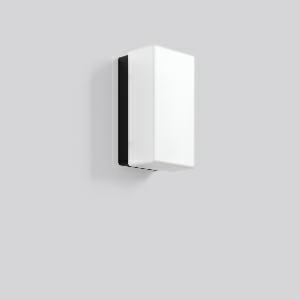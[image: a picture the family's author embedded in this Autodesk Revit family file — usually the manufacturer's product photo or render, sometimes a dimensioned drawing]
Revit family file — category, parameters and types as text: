
# Revit family: rechteck_21146_003_5e70
name_source: partatom
category: Lighting Fixtures
units: mm (PartAtom-declared; Revit-internal decimal feet)

## family parameters
Cut with Voids When Loaded = No
Host = Face
Light Source = No
Part Type = Normal
Room Calculation Point = No
Round Connector Dimension = Use Diameter
Shared = No

## types (1)
- RECHTECK (1 x QA60/clear E27, 700 lm, 46 W, 3000)
    Apparent Load = 46 VA
    CIE Flux Codes = 35 64 86 74 50
    Color Rendering = 90
    Color Temperature = 3000
    Default Elevation = 1800 mm
    Description = Series: RECHTECK
Rectangular surface-mounted luminaire in classic design. Base: plastic. Opal glass: mouth-blown, satin finish. Diffuser fastening: spring system. Suitable for Ceiling mounting, Wall (surface). IP 43 ceiling mounting, IP 44 wall mounting. 
Colour: black
Length: 220 mm
Width: 120 mm
Height: 105 mm
Lamp: A60
Number of lamps: 1
Wattage: 60 W
Socket: E27
System power: 46 W
Rated luminous flux: 350 lm
Luminous efficiency: 8 lm/W
Control gear: Converter not necessary
Protection class: II
Type of protection: IP 43
    Height = 105 mm
    Lamp = 1 x QA60/clear E27
    Lamp Light Flux = 700 lm
    Lamp Power = 46 W
    Lamp count = 1
    Length = 220 mm
    Lifetime = 3000 h
    Luminous efficacy = 8 lm/W
    Manufacturer = RZB
    ModVariant = No
    Model = 21146.003
    Mounting Place = Ceiling, Wall
    Mounting Type = Surface mounted
    Number of Poles = 1
    OnlyDefault = Yes
    Power Factor = 1
    Product Name = RECHTECK
    Product group = Surface mounted ceiling and wall luminaires
    ProductGroupID = 305
    Protection Class = Protection class II
    Protection Degree = IP 43
    RLX_Detail_Level = 1
    RLX_Emergency_Light_Flux = 0 lm
    RLX_Emergency_Type = 0
    RLX_Emergency_Type_DB = No
    RlxData = <blob elided: 20105 chars, md5=e82a3bbe>
    Socket = E27
    Standby Power = 0 W
    System Light Flux = 352 lm
    System Power = 46 W
    Type Comments = Product without accessories
    Type Image = 21146.003.jpg
    URL = http://relux.com
    VarID = ---
    Voltage = 230 V
    Voltage Range = 220-240 V
    Weight = 0.00 kg
    Width = 120 mm

## geometry (parser evidence)
native form markers: Blend x4, Sweep x12
no freeform markers — native parametric forms only
